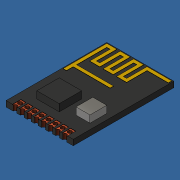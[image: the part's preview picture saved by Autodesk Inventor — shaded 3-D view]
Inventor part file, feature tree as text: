
AUTODESK INVENTOR PART (.ipt)
format: ipt  version: 2018 (Build 220112000, 112)  size: 231,424 bytes
history: native  units: mm
features: extrude x5, sketch x5, hole x1, pattern_linear x1
ambient origin geometry x8: Origin, YZ Plane, XZ Plane, XY Plane, X Axis, Y Axis, Z Axis, Center Point
bodies: Volumenkörper1 (feature_tree)
feature tree (12):
  extrude  "Extrusion1"  Depth=18.0mm
  sketch  "Skizze2"  dims[d2=1.0mm d3=0.0mm d4=1.6mm]
  extrude  "Extrusion2"  Depth=1.6mm
  hole  "Bohrung1"  [1 undecoded]
  pattern_linear  "Rechteckige Anordnung1"  Spacing1=0.05mm  [1 undecoded]
  extrude  "Extrusion3"  Depth=0.7mm
  extrude  "Extrusion4"  Depth=1.27mm
  extrude  "Extrusion5"  Depth=0.2mm
  sketch  "Skizze1"  dims[d0=12.0mm d1=18.0mm]
  sketch  "Skizze3"  dims[d5=0.9mm d6=0.7mm]
  sketch  "Skizze4"  dims[d7=0.9mm]
  sketch  "Skizze5"  dims[d8=1.5mm d9=0.05mm d10=0.0mm d11=0.7mm d12=6.0mm d13=4.0mm d14=2.0mm d15=90.0deg d16=8.0mm d17=20.594885mm d18=80.0mm d20=1.27mm d21=0.2mm d22=0.2mm d23=0.2mm d24=11.5mm d25=0.6mm d26=0.6mm d27=0.6mm d28=0.6mm d29=0.6mm d30=0.6mm d31=4.25mm d32=0.0mm d33=10.0mm d34=0.05mm d35=0.0mm d36=3.0mm d37=2.5mm d38=4.0mm d39=4.0mm d40=1.27mm d41=0.0mm d42=3.0mm d43=2.5mm d44=4.0mm d45=1.0mm d46=1.27mm d47=0.0mm]
note: 2 required parameter values undecoded (feature->parameter linkage not recoverable at this tier; creation-order binding heuristic only, values carry confidence <= 0.55)
